# Revit family: Sanitary_Other-Sanitary_AXOR_48441USA-AXOR-One-Single-lever-bath-mixe_
name_source: partatom
category: Plumbing Fixtures
revit_build: Autodesk Revit 2018 (Build: 20170223_1515(x64)
units: mm (PartAtom-declared; Revit-internal decimal feet)

## family parameters
Always vertical = No
Cut with Voids When Loaded = No
OmniClass Number = 23.40.20.00
OmniClass Title = General Furniture and Specialties
Part Type = Normal
Room Calculation Point = No
Round Connector Dimension = Use Diameter
Shared = No
Work Plane-Based = Yes

## types (2) — shared parameters
Always visible = Yes
BIMobject category = Other Sanitary
Default Elevation = 1219.2 mm  [stored 4 ft]
Design country = Germany
EAN code = 4059625330869
Edition number = 1
IFC Classification = Sanitary Terminal
Installation instructions = https://www.axor-design.com
Manufacturer country = Germany
Manufacturer name = AXOR
Material 2 = AXOR - AXOR One - Graphite
Material main = Chrome
Product Guid = a068b796-c675-4428-b7c0-ad10a4c91512
Product SKU = 48441USA
Product data url = https://www.bimobject.com
Product family = AXOR One
Product group = Bath mixers
Product name = 48441USA AXOR One Single lever bath mixer floor-standing
Product url = https://www.axor-design.com
QR code = https://www.bimobject.com
Technical description = https://www.axor-design.com

## per-type parameters (varying)
| type | Material 1 |
| 671 Matte Black | AXOR - AXOR One - 671 Matte Black |
| 001 Chrome | AXOR - AXOR One - 001 Chrome |

note: [stored X ft] marks values corroborated as IEEE doubles in the binary element streams (Revit-internal decimal feet)

## geometry (parser evidence)
native form markers: Sweep x2
no freeform markers — native parametric forms only
